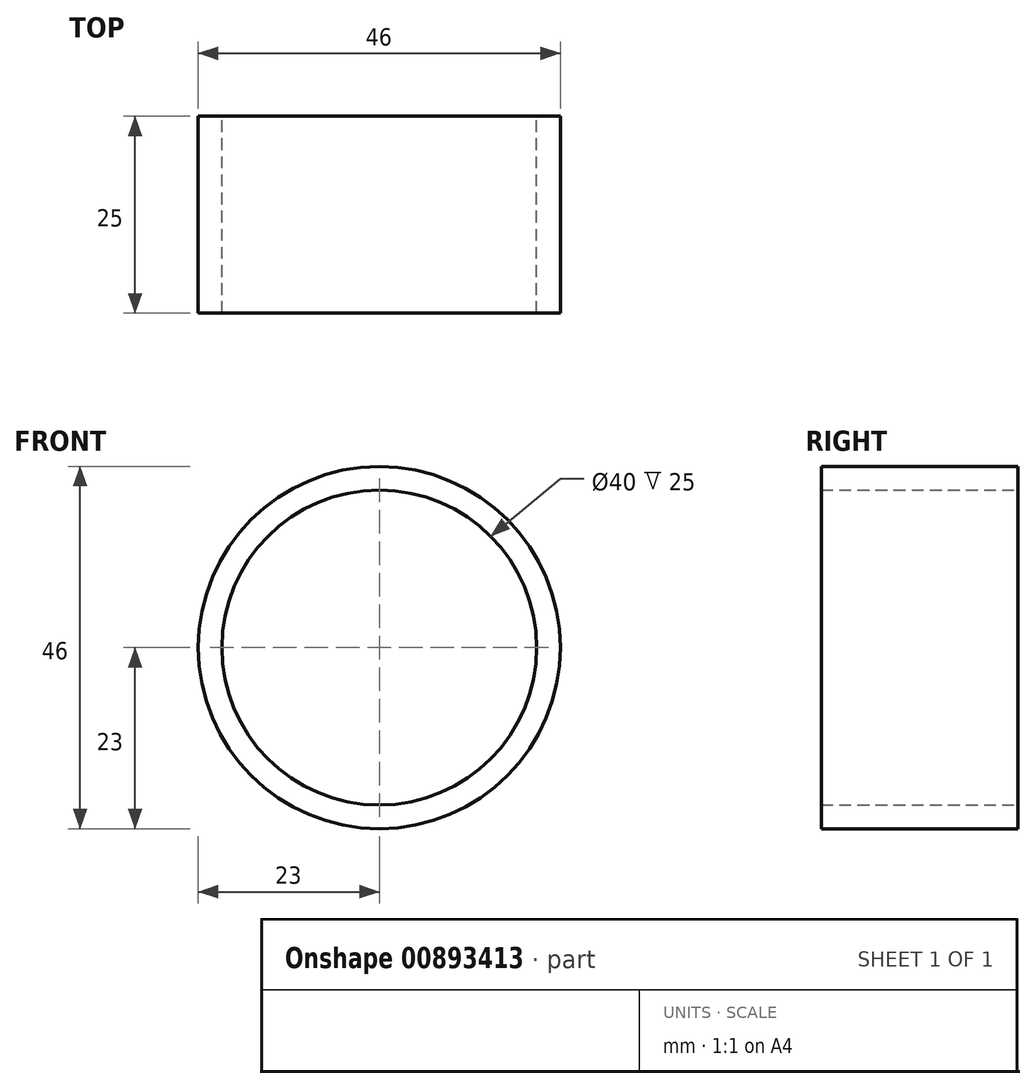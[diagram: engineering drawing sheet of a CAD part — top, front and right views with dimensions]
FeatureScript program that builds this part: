
annotation { "Feature Type Name" : "Feature", "Feature Type Description" : "" }
export const myFeature = defineFeature(function(context is Context, id is Id, definition is map)
    precondition{}
    {
        {
            assignVariable(context, id + "F0", {"name" : "H_rouleau", "anyValue" : 25});
        }
        {
            var Q0;
            Q0=qCreatedBy(makeId("Front.planeOp"),FACE);
            var sketch = newSketch(context, id + "F1", { "sketchPlane" : qUnion([Q0])});
            skCircle(sketch, "E0", {"center": v(0, 0) * mm, "radius": 20 * mm});
            skCircle(sketch, "E1.0", {"center": v(0, 0) * mm, "radius": 23 * mm});
            skSolve(sketch);
        }
        {
            var Q0;
            Q0=makeQuery(id+"F1.imprint","IMPRINT",FACE,{"disambiguationData":[TD([[makeQuery(id+"F1.imprint","IMPRINT",EDGE,{"derivedFrom":sQuery(id+"F1.wireOp",EDGE,"E0")}),-1.0]])]});
            extrude(context, id + "F2", {"entities" : qUnion([Q0]), "depth" : (getVariable(context, 'H_rouleau')) * mm, "offsetDistance" : 25 * mm});
        }
    });
